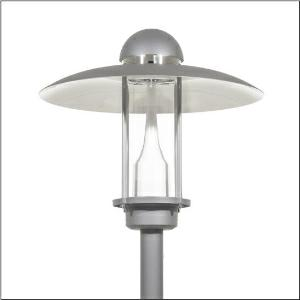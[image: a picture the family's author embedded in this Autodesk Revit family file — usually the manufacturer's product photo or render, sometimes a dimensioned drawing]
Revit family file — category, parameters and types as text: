
# Revit family: city-light_elegance_iq___p1_0a_5xa5265nf14h_5982
name_source: partatom
category: Lighting Fixtures
units: mm (PartAtom-declared; Revit-internal decimal feet)

## family parameters
Cut with Voids When Loaded = No
Host = Face
Light Source = No
Part Type = Normal
Room Calculation Point = No
Round Connector Dimension = Use Diameter
Shared = No

## types (1)
- --- (1 x LED, 1440 lm, 11.8 W, 2700K)
    Apparent Load = 12 VA
    CIE Flux Codes = 32 62 91 97 100
    Color Rendering = 70
    Color Temperature = 2700K
    Default Elevation = 1800 mm
    Description = City-Light Elegance iQ, mast luminaire, Module 540 iQ-SR, primary light control with 3 zone facetted reflector, of plastic, silver coated, highly specular, structured, primary optical cover: cover, of PMMA, transparent, light distribution: P1.0a, light emission: direct distribution, primary light characteristic: strongly asymmetric, installation type: post-top, LED, High Power LED, rated luminous flux: 1.440lm, luminous efficacy: 122lm/W, light colour: 727, colour temperature: 2700K, control gear: ECG iQ, control: presetting dimming logarithmic, Street-Remote, Auto-Match, Temp-Guard, Lumen-Switch, Night-Set, Smart-Wire, Light-Fading, Desk-Remote (wireless, voltage-free reading and setting of iQ features in the workshop via application-optimized NFC function/RFID function), optimised constant luminous flux control (CLO 2.0), with terminal, 6-pole, max. 2.5mm², mains connection: 230..240V, AC, 50/60Hz, start of lifetime: 12W, end of service life: 12W, reduction: 6W, luminaire housing, upper part, of aluminium, coated, Siteco® metallic grey (DB 702S), diameter: 750mm, height: 675mm, spigot size: d x l = 76 x 70mm (post-top) | with reducer (optional accessory) 60 x 70mm, post-top mast mounting element, of diecast aluminium, coated, Siteco® metallic grey (DB 702S), Module 540 iQ-SR, traffic white (RAL 9016), equipment: standard, protection rating (complete): IP65, insulation class (complete): insulation class II (safety insulation), certification: CE, ENEC, VDE, packaging unit: 1 piece

Light Distribution: P1.0a
    Height = 675 mm
    Lamp = 1 x LED
    Lamp Light Flux = 1440 lm
    Lamp Power = 11.8 W
    Lamp count = 1
    Length = 750 mm
    Luminous efficacy = 122 lm/W
    Manufacturer = Siteco
    ModVariant = No
    Model = 5XA5265NF14H
    Number of Poles = 1
    OnlyDefault = Yes
    Power Factor = 1
    Product Name = City-Light Elegance iQ | P1.0a
    Product group = mast luminaire | pylon top
    ProductGroupID = 6100
    Protection Class = Protection class II
    Protection Degree = IP 65
    RLX_Detail_Level = 1
    RLX_Emergency_Light_Flux = 0 lm
    RLX_Emergency_Type = 0
    RLX_Emergency_Type_DB = No
    RlxData = <blob elided: 101777 chars, md5=1a97ea33>
    Socket = socket
    Standby Power = 0 W
    System Light Flux = 1440 lm
    System Power = 12 W
    Type Comments = factory setting: luminous flux: 100 % | dim-lin: 254 | 472 mA
    Type Image = l_1006912.jpg
    URL = http://relux.com
    VarID = @adj_103371
    Voltage = 0 V
    Weight = 0.00 kg
    Width = 0 mm  [stored 0 ft]

note: [stored X ft] marks values corroborated as IEEE doubles in the binary element streams (Revit-internal decimal feet)

## geometry (parser evidence)
native form markers: Blend x4, Sweep x12
no freeform markers — native parametric forms only
